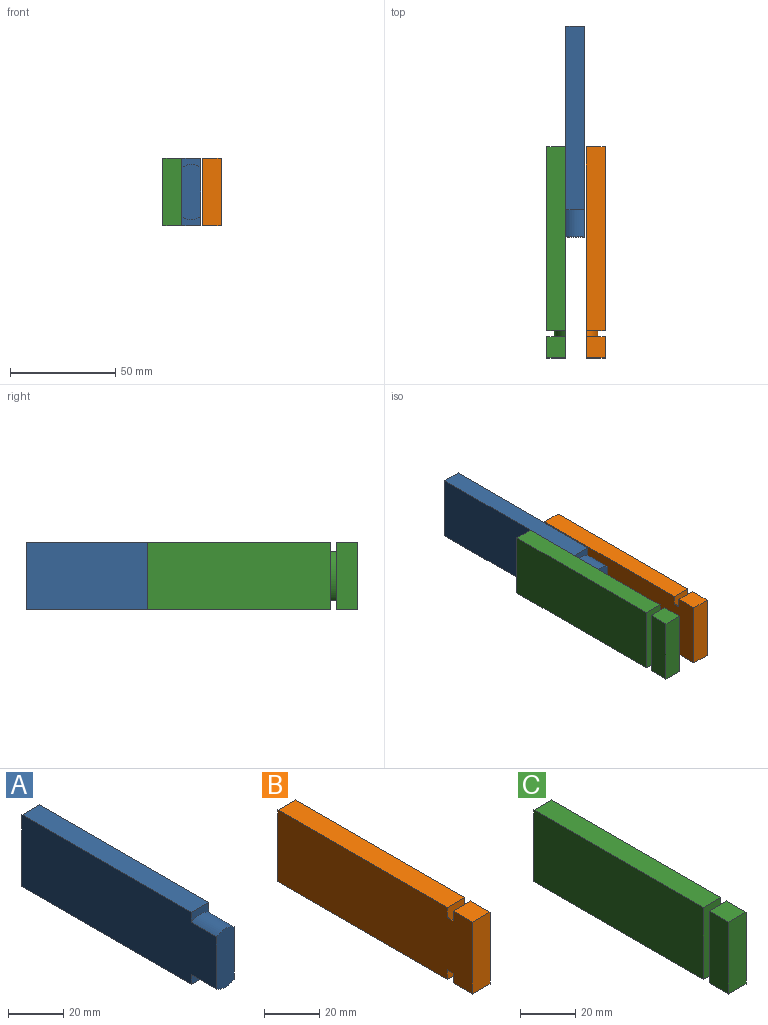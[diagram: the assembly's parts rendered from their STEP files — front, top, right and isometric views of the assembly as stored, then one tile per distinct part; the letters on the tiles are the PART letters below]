
ASSEMBLY  parts=3 mates=2
PART A: 10 faces, bbox 9x100x32 mm
  f0: plane 100x32mm, normal (1,0,0), area 3085.8mm2, adj f1,f3,f4,f5,f6,f7,f8,f9
  f1: plane 26x9mm, normal (0,-1,0), area 225.8mm2, adj f0,f2,f7,f8
  f2: plane 100x32mm, normal (-1,0,0), area 3085.8mm2, adj f1,f3,f4,f5,f6,f7,f8,f9
  f3: plane 87x9mm, normal (0,0,1), area 783mm2, adj f0,f2,f4,f9
  f4: plane 9x4.39mm, normal (0,-1,0), area 31.1mm2, adj f0,f2,f3,f8
  f5: plane 87x9mm, normal (0,0,-1), area 783mm2, adj f0,f2,f6,f9
  f6: plane 9x4.39mm, normal (0,-1,0), area 31.1mm2, adj f0,f2,f5,f7
  f7: extruded ~13x9mm, area 124.2mm2, adj f0,f1,f2,f6
  f8: extruded ~13x9mm, area 124.2mm2, adj f0,f1,f2,f4
  f9: plane 32x9mm, normal (0,1,0), area 288mm2, adj f0,f2,f3,f5
PART B: 12 faces, bbox 9x100x32 mm
  f0: plane 87x9mm, normal (0,0,-1), area 783mm2, adj f1,f3,f4,f11
  f1: plane 87x32mm, normal (1,0,0), area 2784mm2, adj f0,f2,f3,f4
  f2: plane 87x9mm, normal (0,0,1), area 783mm2, adj f1,f3,f4,f11
  f3: plane 32x9mm, normal (0,1,0), area 288mm2, adj f0,f1,f2,f11
  f4: plane 32x9mm, normal (0,-1,0), area 196.7mm2, adj f0,f1,f2,f6,f11
  f5: plane 32x9mm, normal (0,1,0), area 196.7mm2, adj f6,f8,f9,f10,f11
  f6: extruded ~23.22x5.5mm, area 80.2mm2, adj f4,f5,f11
  f7: plane 32x9mm, normal (0,-1,0), area 288mm2, adj f8,f9,f10,f11
  f8: plane 10x9mm, normal (0,0,1), area 90mm2, adj f5,f7,f9,f11
  f9: plane 32x10mm, normal (1,0,0), area 320mm2, adj f5,f7,f8,f10
  f10: plane 10x9mm, normal (0,0,-1), area 90mm2, adj f5,f7,f9,f11
  f11: plane 100x32mm, normal (-1,0,0), area 3173.7mm2, adj f0,f2,f3,f4,f5,f6,f7,f8
PART C: 12 faces, bbox 9x100x32 mm
  f0: plane 32x9mm, normal (0,1,0), area 288mm2, adj f7,f8,f9,f11
  f1: extruded ~23.22x5.5mm, area 80.2mm2, adj f5,f6,f11
  f2: plane 10x9mm, normal (0,0,1), area 90mm2, adj f4,f5,f10,f11
  f3: plane 10x9mm, normal (0,0,-1), area 90mm2, adj f4,f5,f10,f11
  f4: plane 32x9mm, normal (0,-1,0), area 288mm2, adj f2,f3,f10,f11
  f5: plane 32x9mm, normal (0,1,0), area 196.7mm2, adj f1,f2,f3,f10,f11
  f6: plane 32x9mm, normal (0,-1,0), area 196.7mm2, adj f1,f7,f8,f9,f11
  f7: plane 87x9mm, normal (0,0,1), area 783mm2, adj f0,f6,f9,f11
  f8: plane 87x9mm, normal (0,0,-1), area 783mm2, adj f0,f6,f9,f11
  f9: plane 87x32mm, normal (-1,0,0), area 2784mm2, adj f0,f6,f7,f8
  f10: plane 32x10mm, normal (-1,0,0), area 320mm2, adj f2,f3,f4,f5
  f11: plane 100x32mm, normal (1,0,0), area 3173.7mm2, adj f0,f1,f2,f3,f4,f5,f6,f7
PLACE A t=(0,57.34,0)mm
PLACE B t=(0.66,0,0)mm
PLACE C at identity fixed
MATE slider C.f4 <-> A.f1  axis (0,-1,0) through (-9,0,0)mm
MATE slider B.f11 <-> C.f11  axis (-1,0,0) through (5.16,0,0)mm
